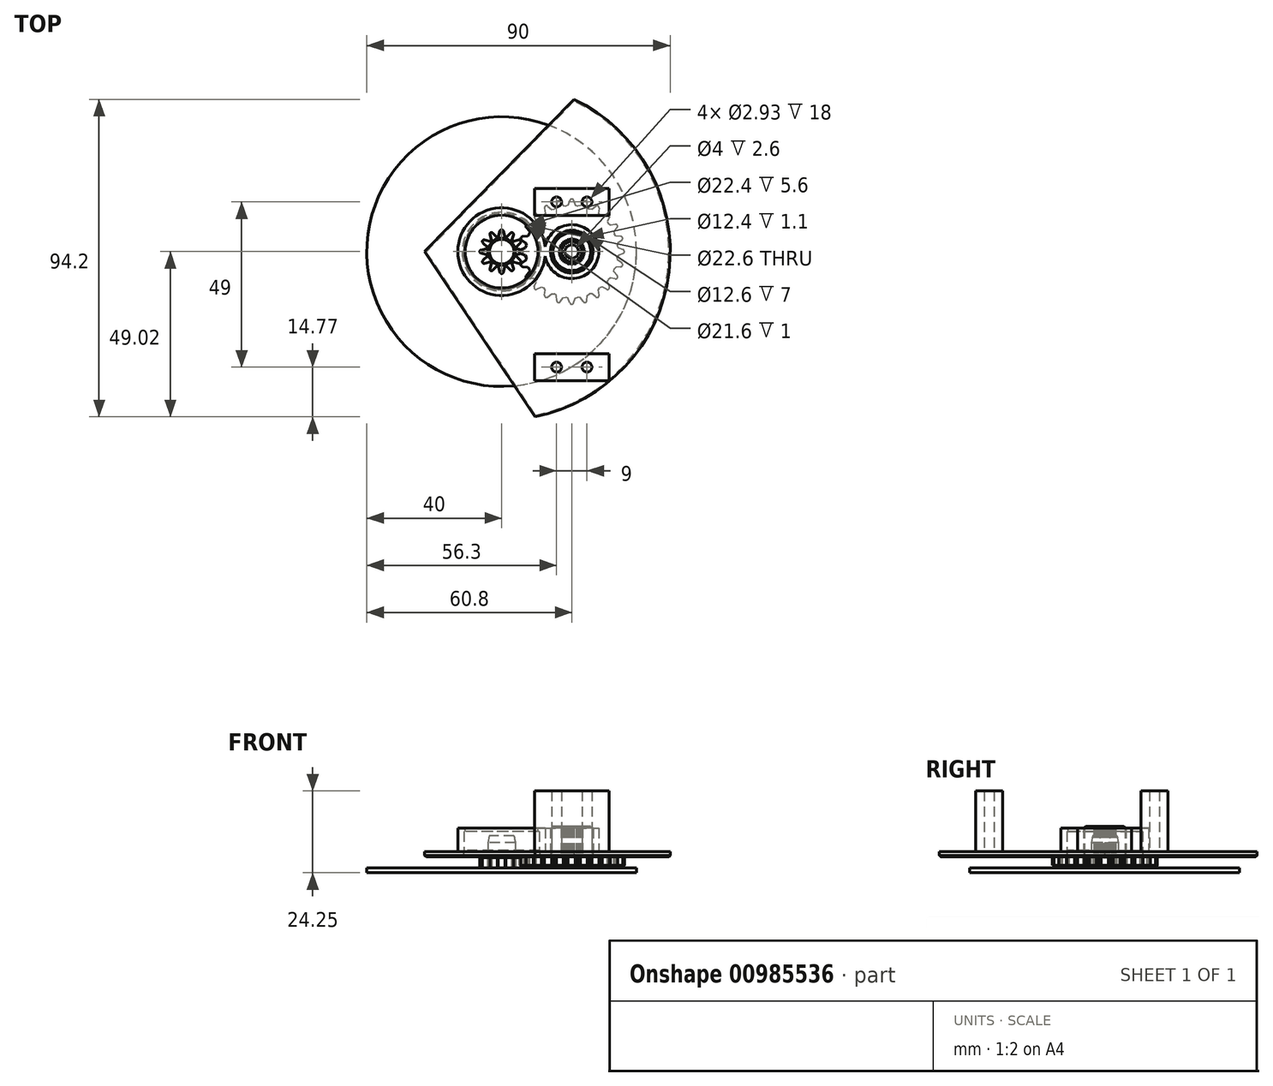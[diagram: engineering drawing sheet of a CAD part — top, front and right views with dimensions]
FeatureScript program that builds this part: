
annotation { "Feature Type Name" : "Feature", "Feature Type Description" : "" }
export const myFeature = defineFeature(function(context is Context, id is Id, definition is map)
    precondition{}
    {
        {
            var Q0;
            Q0=qCreatedBy(makeId("Top.planeOp"),FACE);
            var sketch = newSketch(context, id + "F0", { "sketchPlane" : qUnion([Q0])});
            skCircle(sketch, "E0", {"center": v(0, 0) * mm, "radius": 40 * mm});
            skSolve(sketch);
        }
        {
            var Q0;
            Q0=qSketchRegion(id+"F0",true);
            extrude(context, id + "F1", {"entities" : qUnion([Q0]), "depth" : 1.5 * mm, "offsetDistance" : 25 * mm});
        }
        {
            var Q0;
            Q0=makeQuery(id+"F1.opExtrude","CAP_FACE",FACE,{"disambiguationData":[OSD([sQuery(id+"F0.wireOp",EDGE,"E0")])],"isStart":false});
            var sketch = newSketch(context, id + "F2", { "sketchPlane" : qUnion([Q0])});
            skCircle(sketch, "E1", {"center": v(6, 0) * mm, "radius": 0.5 * mm});
            skLineSegment(sketch, "E2", {"start": v(6.13, 0.48) * mm, "end": v(4.2, 1) * mm});
            skLineSegment(sketch, "E3", {"start": v(4.2, 1) * mm, "end": v(3.85, 2.04) * mm});
            skLineSegment(sketch, "E4.MirrorCS", {"start": v(6.13, -0.48) * mm, "end": v(4.2, -1) * mm});
            skLineSegment(sketch, "E5.MirrorCS", {"start": v(4.2, -1) * mm, "end": v(3.85, -2.04) * mm});
            skCircle(sketch, "E6.1.0", {"center": v(5.2, 3) * mm, "radius": 0.5 * mm});
            skLineSegment(sketch, "E6.1.1", {"start": v(3.13, 2.97) * mm, "end": v(2.31, 3.69) * mm});
            skLineSegment(sketch, "E6.1.2", {"start": v(5.55, 2.65) * mm, "end": v(4.14, 1.23) * mm});
            skLineSegment(sketch, "E6.1.3", {"start": v(4.14, 1.23) * mm, "end": v(4.35, 0.16) * mm});
            skLineSegment(sketch, "E6.1.4", {"start": v(5.07, 3.48) * mm, "end": v(3.13, 2.97) * mm});
            skCircle(sketch, "E6.2.0", {"center": v(3, 5.2) * mm, "radius": 0.5 * mm});
            skLineSegment(sketch, "E6.2.1", {"start": v(1.23, 4.14) * mm, "end": v(0.16, 4.35) * mm});
            skLineSegment(sketch, "E6.2.2", {"start": v(3.48, 5.07) * mm, "end": v(2.97, 3.13) * mm});
            skLineSegment(sketch, "E6.2.3", {"start": v(2.97, 3.13) * mm, "end": v(3.69, 2.31) * mm});
            skLineSegment(sketch, "E6.2.4", {"start": v(2.65, 5.55) * mm, "end": v(1.23, 4.14) * mm});
            skCircle(sketch, "E6.3.0", {"center": v(0, 6) * mm, "radius": 0.5 * mm});
            skLineSegment(sketch, "E6.3.1", {"start": v(-1, 4.2) * mm, "end": v(-2.04, 3.85) * mm});
            skLineSegment(sketch, "E6.3.2", {"start": v(0.48, 6.13) * mm, "end": v(1, 4.2) * mm});
            skLineSegment(sketch, "E6.3.3", {"start": v(1, 4.2) * mm, "end": v(2.04, 3.85) * mm});
            skLineSegment(sketch, "E6.3.4", {"start": v(-0.48, 6.13) * mm, "end": v(-1, 4.2) * mm});
            skCircle(sketch, "E6.4.0", {"center": v(-3, 5.2) * mm, "radius": 0.5 * mm});
            skLineSegment(sketch, "E6.4.1", {"start": v(-2.97, 3.13) * mm, "end": v(-3.69, 2.31) * mm});
            skLineSegment(sketch, "E6.4.2", {"start": v(-2.65, 5.55) * mm, "end": v(-1.23, 4.14) * mm});
            skLineSegment(sketch, "E6.4.3", {"start": v(-1.23, 4.14) * mm, "end": v(-0.16, 4.35) * mm});
            skLineSegment(sketch, "E6.4.4", {"start": v(-3.48, 5.07) * mm, "end": v(-2.97, 3.13) * mm});
            skCircle(sketch, "E6.5.0", {"center": v(-5.2, 3) * mm, "radius": 0.5 * mm});
            skLineSegment(sketch, "E6.5.1", {"start": v(-4.14, 1.23) * mm, "end": v(-4.35, 0.16) * mm});
            skLineSegment(sketch, "E6.5.2", {"start": v(-5.07, 3.48) * mm, "end": v(-3.13, 2.97) * mm});
            skLineSegment(sketch, "E6.5.3", {"start": v(-3.13, 2.97) * mm, "end": v(-2.31, 3.69) * mm});
            skLineSegment(sketch, "E6.5.4", {"start": v(-5.55, 2.65) * mm, "end": v(-4.14, 1.23) * mm});
            skCircle(sketch, "E6.6.0", {"center": v(-6, 0) * mm, "radius": 0.5 * mm});
            skLineSegment(sketch, "E6.6.1", {"start": v(-4.2, -1) * mm, "end": v(-3.85, -2.04) * mm});
            skLineSegment(sketch, "E6.6.2", {"start": v(-6.13, 0.48) * mm, "end": v(-4.2, 1) * mm});
            skLineSegment(sketch, "E6.6.3", {"start": v(-4.2, 1) * mm, "end": v(-3.85, 2.04) * mm});
            skLineSegment(sketch, "E6.6.4", {"start": v(-6.13, -0.48) * mm, "end": v(-4.2, -1) * mm});
            skCircle(sketch, "E6.7.0", {"center": v(-5.2, -3) * mm, "radius": 0.5 * mm});
            skLineSegment(sketch, "E6.7.1", {"start": v(-3.13, -2.97) * mm, "end": v(-2.31, -3.69) * mm});
            skLineSegment(sketch, "E6.7.2", {"start": v(-5.55, -2.65) * mm, "end": v(-4.14, -1.23) * mm});
            skLineSegment(sketch, "E6.7.3", {"start": v(-4.14, -1.23) * mm, "end": v(-4.35, -0.16) * mm});
            skLineSegment(sketch, "E6.7.4", {"start": v(-5.07, -3.48) * mm, "end": v(-3.13, -2.97) * mm});
            skCircle(sketch, "E6.8.0", {"center": v(-3, -5.2) * mm, "radius": 0.5 * mm});
            skLineSegment(sketch, "E6.8.1", {"start": v(-1.23, -4.14) * mm, "end": v(-0.16, -4.35) * mm});
            skLineSegment(sketch, "E6.8.2", {"start": v(-3.48, -5.07) * mm, "end": v(-2.97, -3.13) * mm});
            skLineSegment(sketch, "E6.8.3", {"start": v(-2.97, -3.13) * mm, "end": v(-3.69, -2.31) * mm});
            skLineSegment(sketch, "E6.8.4", {"start": v(-2.65, -5.55) * mm, "end": v(-1.23, -4.14) * mm});
            skCircle(sketch, "E6.9.0", {"center": v(0, -6) * mm, "radius": 0.5 * mm});
            skLineSegment(sketch, "E6.9.1", {"start": v(1, -4.2) * mm, "end": v(2.04, -3.85) * mm});
            skLineSegment(sketch, "E6.9.2", {"start": v(-0.48, -6.13) * mm, "end": v(-1, -4.2) * mm});
            skLineSegment(sketch, "E6.9.3", {"start": v(-1, -4.2) * mm, "end": v(-2.04, -3.85) * mm});
            skLineSegment(sketch, "E6.9.4", {"start": v(0.48, -6.13) * mm, "end": v(1, -4.2) * mm});
            skPoint(sketch, "E6.center", {"position": v(0, 0) * mm});
            skLineSegment(sketch, "E7.2.10.0", {"start": v(2.97, -3.13) * mm, "end": v(3.69, -2.31) * mm});
            skLineSegment(sketch, "E7.5.10.0", {"start": v(2.65, -5.55) * mm, "end": v(1.23, -4.14) * mm});
            skLineSegment(sketch, "E7.8.10.0", {"start": v(1.23, -4.14) * mm, "end": v(0.16, -4.35) * mm});
            skCircle(sketch, "E7.10.10.0", {"center": v(3, -5.2) * mm, "radius": 0.5 * mm});
            skLineSegment(sketch, "E7.11.10.0", {"start": v(3.48, -5.07) * mm, "end": v(2.97, -3.13) * mm});
            skLineSegment(sketch, "E7.2.11.0", {"start": v(4.14, -1.23) * mm, "end": v(4.35, -0.16) * mm});
            skLineSegment(sketch, "E7.5.11.0", {"start": v(5.07, -3.48) * mm, "end": v(3.13, -2.97) * mm});
            skLineSegment(sketch, "E7.8.11.0", {"start": v(3.13, -2.97) * mm, "end": v(2.31, -3.69) * mm});
            skCircle(sketch, "E7.10.11.0", {"center": v(5.2, -3) * mm, "radius": 0.5 * mm});
            skLineSegment(sketch, "E7.11.11.0", {"start": v(5.55, -2.65) * mm, "end": v(4.14, -1.23) * mm});
            skSolve(sketch);
        }
        {
            var Q0;
            Q0=qSketchRegion(id+"F2",true);
            extrude(context, id + "F3", {"entities" : qUnion([Q0]), "operationType" : NewBodyOperationType.ADD, "depth" : 3 * mm, "offsetDistance" : 25 * mm});
        }
        {
            var Q0;
            Q0=makeQuery(id+"F3.opExtrude","CAP_FACE",FACE,{"disambiguationData":[OSD([sQuery(id+"F2.wireOp",EDGE,"E1"),sQuery(id+"F2.wireOp",EDGE,"E2"),sQuery(id+"F2.wireOp",EDGE,"E3"),sQuery(id+"F2.wireOp",EDGE,"E4.MirrorCS"),sQuery(id+"F2.wireOp",EDGE,"E5.MirrorCS"),sQuery(id+"F2.wireOp",EDGE,"E6.1.0"),sQuery(id+"F2.wireOp",EDGE,"E6.1.1"),sQuery(id+"F2.wireOp",EDGE,"E6.1.2"),sQuery(id+"F2.wireOp",EDGE,"E6.1.3"),sQuery(id+"F2.wireOp",EDGE,"E6.1.4"),sQuery(id+"F2.wireOp",EDGE,"E6.2.0"),sQuery(id+"F2.wireOp",EDGE,"E6.2.1"),sQuery(id+"F2.wireOp",EDGE,"E6.2.2"),sQuery(id+"F2.wireOp",EDGE,"E6.2.3"),sQuery(id+"F2.wireOp",EDGE,"E6.2.4"),sQuery(id+"F2.wireOp",EDGE,"E6.3.0"),sQuery(id+"F2.wireOp",EDGE,"E6.3.1"),sQuery(id+"F2.wireOp",EDGE,"E6.3.2"),sQuery(id+"F2.wireOp",EDGE,"E6.3.3"),sQuery(id+"F2.wireOp",EDGE,"E6.3.4"),sQuery(id+"F2.wireOp",EDGE,"E6.4.0"),sQuery(id+"F2.wireOp",EDGE,"E6.4.1"),sQuery(id+"F2.wireOp",EDGE,"E6.4.2"),sQuery(id+"F2.wireOp",EDGE,"E6.4.3"),sQuery(id+"F2.wireOp",EDGE,"E6.4.4"),sQuery(id+"F2.wireOp",EDGE,"E6.5.0"),sQuery(id+"F2.wireOp",EDGE,"E6.5.1"),sQuery(id+"F2.wireOp",EDGE,"E6.5.2"),sQuery(id+"F2.wireOp",EDGE,"E6.5.3"),sQuery(id+"F2.wireOp",EDGE,"E6.5.4"),sQuery(id+"F2.wireOp",EDGE,"E6.6.0"),sQuery(id+"F2.wireOp",EDGE,"E6.6.1"),sQuery(id+"F2.wireOp",EDGE,"E6.6.2"),sQuery(id+"F2.wireOp",EDGE,"E6.6.3"),sQuery(id+"F2.wireOp",EDGE,"E6.6.4"),sQuery(id+"F2.wireOp",EDGE,"E6.7.0"),sQuery(id+"F2.wireOp",EDGE,"E6.7.1"),sQuery(id+"F2.wireOp",EDGE,"E6.7.2"),sQuery(id+"F2.wireOp",EDGE,"E6.7.3"),sQuery(id+"F2.wireOp",EDGE,"E6.7.4"),sQuery(id+"F2.wireOp",EDGE,"E6.8.0"),sQuery(id+"F2.wireOp",EDGE,"E6.8.1"),sQuery(id+"F2.wireOp",EDGE,"E6.8.2"),sQuery(id+"F2.wireOp",EDGE,"E6.8.3"),sQuery(id+"F2.wireOp",EDGE,"E6.8.4"),sQuery(id+"F2.wireOp",EDGE,"E6.9.0"),sQuery(id+"F2.wireOp",EDGE,"E6.9.1"),sQuery(id+"F2.wireOp",EDGE,"E6.9.2"),sQuery(id+"F2.wireOp",EDGE,"E6.9.3"),sQuery(id+"F2.wireOp",EDGE,"E6.9.4"),sQuery(id+"F2.wireOp",EDGE,"E7.2.10.0"),sQuery(id+"F2.wireOp",EDGE,"E7.5.10.0"),sQuery(id+"F2.wireOp",EDGE,"E7.8.10.0"),sQuery(id+"F2.wireOp",EDGE,"E7.10.10.0"),sQuery(id+"F2.wireOp",EDGE,"E7.11.10.0"),sQuery(id+"F2.wireOp",EDGE,"E7.2.11.0"),sQuery(id+"F2.wireOp",EDGE,"E7.5.11.0"),sQuery(id+"F2.wireOp",EDGE,"E7.8.11.0"),sQuery(id+"F2.wireOp",EDGE,"E7.10.11.0"),sQuery(id+"F2.wireOp",EDGE,"E7.11.11.0")])],"isStart":false});
            var sketch = newSketch(context, id + "F4", { "sketchPlane" : qUnion([Q0])});
            skCircle(sketch, "E8", {"center": v(0, 0) * mm, "radius": 4.05 * mm});
            skSolve(sketch);
        }
        {
            var Q0;
            Q0=qSketchRegion(id+"F4",true);
            extrude(context, id + "F5", {"entities" : qUnion([Q0]), "operationType" : NewBodyOperationType.ADD, "depth" : 6.5 * mm, "offsetDistance" : 25 * mm});
        }
        {
            var Q0;
            Q0=makeQuery(id+"F5.opExtrude","CAP_EDGE",EDGE,{"disambiguationData":[OSD([sQuery(id+"F4.wireOp",EDGE,"E8")])],"isStart":false});
            chamfer(context, id + "F6", {"entities" : qUnion([Q0]), "chamferType" : ChamferType.TWO_OFFSETS, "width1" : .4 * mm, "oppositeDirection" : false, "width2" : 2 * mm, "tangentPropagation" : true});
        }
        {
            var Q0;
            Q0=makeQuery(id+"F5.opExtrude","CAP_FACE",FACE,{"disambiguationData":[OSD([sQuery(id+"F4.wireOp",EDGE,"E8")])],"isStart":false});
            cPlane(context, id + "F7", {"entities" : qUnion([Q0]), "cplaneType" : CPlaneType.OFFSET, "offset" : 6.25 * mm, "oppositeDirection" : true, "width" : 150 * mm, "height" : 150 * mm});
        }
        {
            var Q0;
            Q0=qCreatedBy(id+"F7.planeOp",FACE);
            var sketch = newSketch(context, id + "F8", { "sketchPlane" : qUnion([Q0])});
            skCircle(sketch, "E9", {"center": v(20.8, 0) * mm, "radius": 2 * mm});
            skCircle(sketch, "E10", {"center": v(35.8, 0) * mm, "radius": 0.6 * mm});
            skLineSegment(sketch, "E11", {"start": v(36, 0.56) * mm, "end": v(34.6, 1.08) * mm});
            skLineSegment(sketch, "E12", {"start": v(35.8, 0) * mm, "end": v(35.3, 0) * mm});
            skLineSegment(sketch, "E13", {"start": v(34.6, 1.08) * mm, "end": v(34.2, 2) * mm});
            skLineSegment(sketch, "E14.MirrorCS", {"start": v(36, -0.56) * mm, "end": v(34.6, -1.08) * mm});
            skLineSegment(sketch, "E15.MirrorCS", {"start": v(34.6, -1.08) * mm, "end": v(34.2, -2) * mm});
            skLineSegment(sketch, "E16.1.0", {"start": v(35.63, 3.4) * mm, "end": v(34.4, 2.53) * mm});
            skCircle(sketch, "E16.1.1", {"center": v(35.29, 3.88) * mm, "radius": 0.6 * mm});
            skLineSegment(sketch, "E16.1.2", {"start": v(35.34, 4.48) * mm, "end": v(33.85, 4.61) * mm});
            skLineSegment(sketch, "E16.1.3", {"start": v(34.4, 2.53) * mm, "end": v(34.25, 1.54) * mm});
            skLineSegment(sketch, "E16.1.4", {"start": v(33.85, 4.61) * mm, "end": v(33.22, 5.4) * mm});
            skLineSegment(sketch, "E16.1.5", {"start": v(35.29, 3.88) * mm, "end": v(34.8, 3.75) * mm});
            skLineSegment(sketch, "E16.2.0", {"start": v(34.25, 7.11) * mm, "end": v(33.29, 5.97) * mm});
            skCircle(sketch, "E16.2.1", {"center": v(33.8, 7.5) * mm, "radius": 0.6 * mm});
            skLineSegment(sketch, "E16.2.2", {"start": v(33.69, 8.1) * mm, "end": v(32.2, 7.83) * mm});
            skLineSegment(sketch, "E16.2.3", {"start": v(33.29, 5.97) * mm, "end": v(33.4, 4.97) * mm});
            skLineSegment(sketch, "E16.2.4", {"start": v(32.2, 7.83) * mm, "end": v(31.4, 8.42) * mm});
            skLineSegment(sketch, "E16.2.5", {"start": v(33.8, 7.5) * mm, "end": v(33.36, 7.25) * mm});
            skLineSegment(sketch, "E16.3.0", {"start": v(31.95, 10.35) * mm, "end": v(31.32, 9) * mm});
            skCircle(sketch, "E16.3.1", {"center": v(31.4, 10.6) * mm, "radius": 0.6 * mm});
            skLineSegment(sketch, "E16.3.2", {"start": v(31.15, 11.15) * mm, "end": v(29.8, 10.52) * mm});
            skLineSegment(sketch, "E16.3.3", {"start": v(31.32, 9) * mm, "end": v(31.68, 8.06) * mm});
            skLineSegment(sketch, "E16.3.4", {"start": v(29.8, 10.52) * mm, "end": v(28.86, 10.88) * mm});
            skLineSegment(sketch, "E16.3.5", {"start": v(31.4, 10.6) * mm, "end": v(31.05, 10.25) * mm});
            skLineSegment(sketch, "E16.4.0", {"start": v(28.9, 12.89) * mm, "end": v(28.63, 11.4) * mm});
            skCircle(sketch, "E16.4.1", {"center": v(28.3, 13) * mm, "radius": 0.6 * mm});
            skLineSegment(sketch, "E16.4.2", {"start": v(27.91, 13.45) * mm, "end": v(26.77, 12.49) * mm});
            skLineSegment(sketch, "E16.4.3", {"start": v(28.63, 11.4) * mm, "end": v(29.22, 10.6) * mm});
            skLineSegment(sketch, "E16.4.4", {"start": v(26.77, 12.49) * mm, "end": v(25.77, 12.6) * mm});
            skLineSegment(sketch, "E16.4.5", {"start": v(28.3, 13) * mm, "end": v(28.05, 12.56) * mm});
            skLineSegment(sketch, "E16.5.0", {"start": v(25.28, 14.54) * mm, "end": v(25.41, 13.05) * mm});
            skCircle(sketch, "E16.5.1", {"center": v(24.68, 14.49) * mm, "radius": 0.6 * mm});
            skLineSegment(sketch, "E16.5.2", {"start": v(24.2, 14.83) * mm, "end": v(23.33, 13.6) * mm});
            skLineSegment(sketch, "E16.5.3", {"start": v(25.41, 13.05) * mm, "end": v(26.2, 12.42) * mm});
            skLineSegment(sketch, "E16.5.4", {"start": v(23.33, 13.6) * mm, "end": v(22.34, 13.45) * mm});
            skLineSegment(sketch, "E16.5.5", {"start": v(24.68, 14.49) * mm, "end": v(24.55, 14) * mm});
            skLineSegment(sketch, "E16.6.0", {"start": v(21.36, 15.2) * mm, "end": v(21.88, 13.8) * mm});
            skCircle(sketch, "E16.6.1", {"center": v(20.8, 15) * mm, "radius": 0.6 * mm});
            skLineSegment(sketch, "E16.6.2", {"start": v(20.24, 15.2) * mm, "end": v(19.72, 13.8) * mm});
            skLineSegment(sketch, "E16.6.3", {"start": v(21.88, 13.8) * mm, "end": v(22.8, 13.4) * mm});
            skLineSegment(sketch, "E16.6.4", {"start": v(19.72, 13.8) * mm, "end": v(18.8, 13.4) * mm});
            skLineSegment(sketch, "E16.6.5", {"start": v(20.8, 15) * mm, "end": v(20.8, 14.5) * mm});
            skLineSegment(sketch, "E16.7.0", {"start": v(17.4, 14.83) * mm, "end": v(18.27, 13.6) * mm});
            skCircle(sketch, "E16.7.1", {"center": v(16.92, 14.49) * mm, "radius": 0.6 * mm});
            skLineSegment(sketch, "E16.7.2", {"start": v(16.32, 14.54) * mm, "end": v(16.19, 13.05) * mm});
            skLineSegment(sketch, "E16.7.3", {"start": v(18.27, 13.6) * mm, "end": v(19.26, 13.45) * mm});
            skLineSegment(sketch, "E16.7.4", {"start": v(16.19, 13.05) * mm, "end": v(15.4, 12.42) * mm});
            skLineSegment(sketch, "E16.7.5", {"start": v(16.92, 14.49) * mm, "end": v(17.05, 14) * mm});
            skLineSegment(sketch, "E16.8.0", {"start": v(13.69, 13.45) * mm, "end": v(14.83, 12.49) * mm});
            skCircle(sketch, "E16.8.1", {"center": v(13.3, 13) * mm, "radius": 0.6 * mm});
            skLineSegment(sketch, "E16.8.2", {"start": v(12.7, 12.89) * mm, "end": v(12.97, 11.4) * mm});
            skLineSegment(sketch, "E16.8.3", {"start": v(14.83, 12.49) * mm, "end": v(15.83, 12.6) * mm});
            skLineSegment(sketch, "E16.8.4", {"start": v(12.97, 11.4) * mm, "end": v(12.38, 10.6) * mm});
            skLineSegment(sketch, "E16.8.5", {"start": v(13.3, 13) * mm, "end": v(13.55, 12.56) * mm});
            skLineSegment(sketch, "E16.9.0", {"start": v(10.45, 11.15) * mm, "end": v(11.8, 10.52) * mm});
            skCircle(sketch, "E16.9.1", {"center": v(10.2, 10.6) * mm, "radius": 0.6 * mm});
            skLineSegment(sketch, "E16.9.2", {"start": v(9.65, 10.35) * mm, "end": v(10.28, 9) * mm});
            skLineSegment(sketch, "E16.9.3", {"start": v(11.8, 10.52) * mm, "end": v(12.74, 10.88) * mm});
            skLineSegment(sketch, "E16.9.4", {"start": v(10.28, 9) * mm, "end": v(9.92, 8.06) * mm});
            skLineSegment(sketch, "E16.9.5", {"start": v(10.2, 10.6) * mm, "end": v(10.55, 10.25) * mm});
            skLineSegment(sketch, "E16.10.0", {"start": v(7.91, 8.1) * mm, "end": v(9.4, 7.83) * mm});
            skCircle(sketch, "E16.10.1", {"center": v(7.8, 7.5) * mm, "radius": 0.6 * mm});
            skLineSegment(sketch, "E16.10.2", {"start": v(7.35, 7.11) * mm, "end": v(8.31, 5.97) * mm});
            skLineSegment(sketch, "E16.10.3", {"start": v(9.4, 7.83) * mm, "end": v(10.2, 8.42) * mm});
            skLineSegment(sketch, "E16.10.4", {"start": v(8.31, 5.97) * mm, "end": v(8.2, 4.97) * mm});
            skLineSegment(sketch, "E16.10.5", {"start": v(7.8, 7.5) * mm, "end": v(8.24, 7.25) * mm});
            skLineSegment(sketch, "E16.11.0", {"start": v(6.26, 4.48) * mm, "end": v(7.75, 4.61) * mm});
            skCircle(sketch, "E16.11.1", {"center": v(6.31, 3.88) * mm, "radius": 0.6 * mm});
            skLineSegment(sketch, "E16.11.2", {"start": v(5.97, 3.4) * mm, "end": v(7.2, 2.53) * mm});
            skLineSegment(sketch, "E16.11.3", {"start": v(7.75, 4.61) * mm, "end": v(8.38, 5.4) * mm});
            skLineSegment(sketch, "E16.11.4", {"start": v(7.2, 2.53) * mm, "end": v(7.35, 1.54) * mm});
            skLineSegment(sketch, "E16.11.5", {"start": v(6.31, 3.88) * mm, "end": v(6.8, 3.75) * mm});
            skLineSegment(sketch, "E16.12.0", {"start": v(5.6, 0.56) * mm, "end": v(7, 1.08) * mm});
            skCircle(sketch, "E16.12.1", {"center": v(5.8, 0) * mm, "radius": 0.6 * mm});
            skLineSegment(sketch, "E16.12.2", {"start": v(5.6, -0.56) * mm, "end": v(7, -1.08) * mm});
            skLineSegment(sketch, "E16.12.3", {"start": v(7, 1.08) * mm, "end": v(7.4, 2) * mm});
            skLineSegment(sketch, "E16.12.4", {"start": v(7, -1.08) * mm, "end": v(7.4, -2) * mm});
            skLineSegment(sketch, "E16.12.5", {"start": v(5.8, 0) * mm, "end": v(6.3, 0) * mm});
            skLineSegment(sketch, "E16.13.0", {"start": v(5.97, -3.4) * mm, "end": v(7.2, -2.53) * mm});
            skCircle(sketch, "E16.13.1", {"center": v(6.31, -3.88) * mm, "radius": 0.6 * mm});
            skLineSegment(sketch, "E16.13.2", {"start": v(6.26, -4.48) * mm, "end": v(7.75, -4.61) * mm});
            skLineSegment(sketch, "E16.13.3", {"start": v(7.2, -2.53) * mm, "end": v(7.35, -1.54) * mm});
            skLineSegment(sketch, "E16.13.4", {"start": v(7.75, -4.61) * mm, "end": v(8.38, -5.4) * mm});
            skLineSegment(sketch, "E16.13.5", {"start": v(6.31, -3.88) * mm, "end": v(6.8, -3.75) * mm});
            skLineSegment(sketch, "E16.14.0", {"start": v(7.35, -7.11) * mm, "end": v(8.31, -5.97) * mm});
            skCircle(sketch, "E16.14.1", {"center": v(7.8, -7.5) * mm, "radius": 0.6 * mm});
            skLineSegment(sketch, "E16.14.2", {"start": v(7.91, -8.1) * mm, "end": v(9.4, -7.83) * mm});
            skLineSegment(sketch, "E16.14.3", {"start": v(8.31, -5.97) * mm, "end": v(8.2, -4.97) * mm});
            skLineSegment(sketch, "E16.14.4", {"start": v(9.4, -7.83) * mm, "end": v(10.2, -8.42) * mm});
            skLineSegment(sketch, "E16.14.5", {"start": v(7.8, -7.5) * mm, "end": v(8.24, -7.25) * mm});
            skLineSegment(sketch, "E16.15.0", {"start": v(9.65, -10.35) * mm, "end": v(10.28, -9) * mm});
            skCircle(sketch, "E16.15.1", {"center": v(10.2, -10.6) * mm, "radius": 0.6 * mm});
            skLineSegment(sketch, "E16.15.2", {"start": v(10.45, -11.15) * mm, "end": v(11.8, -10.52) * mm});
            skLineSegment(sketch, "E16.15.3", {"start": v(10.28, -9) * mm, "end": v(9.92, -8.06) * mm});
            skLineSegment(sketch, "E16.15.4", {"start": v(11.8, -10.52) * mm, "end": v(12.74, -10.88) * mm});
            skLineSegment(sketch, "E16.15.5", {"start": v(10.2, -10.6) * mm, "end": v(10.55, -10.25) * mm});
            skLineSegment(sketch, "E16.16.0", {"start": v(12.7, -12.89) * mm, "end": v(12.97, -11.4) * mm});
            skCircle(sketch, "E16.16.1", {"center": v(13.3, -13) * mm, "radius": 0.6 * mm});
            skLineSegment(sketch, "E16.16.2", {"start": v(13.69, -13.45) * mm, "end": v(14.83, -12.49) * mm});
            skLineSegment(sketch, "E16.16.3", {"start": v(12.97, -11.4) * mm, "end": v(12.38, -10.6) * mm});
            skLineSegment(sketch, "E16.16.4", {"start": v(14.83, -12.49) * mm, "end": v(15.83, -12.6) * mm});
            skLineSegment(sketch, "E16.16.5", {"start": v(13.3, -13) * mm, "end": v(13.55, -12.56) * mm});
            skLineSegment(sketch, "E16.17.0", {"start": v(16.32, -14.54) * mm, "end": v(16.19, -13.05) * mm});
            skCircle(sketch, "E16.17.1", {"center": v(16.92, -14.49) * mm, "radius": 0.6 * mm});
            skLineSegment(sketch, "E16.17.2", {"start": v(17.4, -14.83) * mm, "end": v(18.27, -13.6) * mm});
            skLineSegment(sketch, "E16.17.3", {"start": v(16.19, -13.05) * mm, "end": v(15.4, -12.42) * mm});
            skLineSegment(sketch, "E16.17.4", {"start": v(18.27, -13.6) * mm, "end": v(19.26, -13.45) * mm});
            skLineSegment(sketch, "E16.17.5", {"start": v(16.92, -14.49) * mm, "end": v(17.05, -14) * mm});
            skLineSegment(sketch, "E16.18.0", {"start": v(20.24, -15.2) * mm, "end": v(19.72, -13.8) * mm});
            skCircle(sketch, "E16.18.1", {"center": v(20.8, -15) * mm, "radius": 0.6 * mm});
            skLineSegment(sketch, "E16.18.2", {"start": v(21.36, -15.2) * mm, "end": v(21.88, -13.8) * mm});
            skLineSegment(sketch, "E16.18.3", {"start": v(19.72, -13.8) * mm, "end": v(18.8, -13.4) * mm});
            skLineSegment(sketch, "E16.18.4", {"start": v(21.88, -13.8) * mm, "end": v(22.8, -13.4) * mm});
            skLineSegment(sketch, "E16.18.5", {"start": v(20.8, -15) * mm, "end": v(20.8, -14.5) * mm});
            skLineSegment(sketch, "E16.19.0", {"start": v(24.2, -14.83) * mm, "end": v(23.33, -13.6) * mm});
            skCircle(sketch, "E16.19.1", {"center": v(24.68, -14.49) * mm, "radius": 0.6 * mm});
            skLineSegment(sketch, "E16.19.2", {"start": v(25.28, -14.54) * mm, "end": v(25.41, -13.05) * mm});
            skLineSegment(sketch, "E16.19.3", {"start": v(23.33, -13.6) * mm, "end": v(22.34, -13.45) * mm});
            skLineSegment(sketch, "E16.19.4", {"start": v(25.41, -13.05) * mm, "end": v(26.2, -12.42) * mm});
            skLineSegment(sketch, "E16.19.5", {"start": v(24.68, -14.49) * mm, "end": v(24.55, -14) * mm});
            skLineSegment(sketch, "E16.20.0", {"start": v(27.91, -13.45) * mm, "end": v(26.77, -12.49) * mm});
            skCircle(sketch, "E16.20.1", {"center": v(28.3, -13) * mm, "radius": 0.6 * mm});
            skLineSegment(sketch, "E16.20.2", {"start": v(28.9, -12.89) * mm, "end": v(28.63, -11.4) * mm});
            skLineSegment(sketch, "E16.20.3", {"start": v(26.77, -12.49) * mm, "end": v(25.77, -12.6) * mm});
            skLineSegment(sketch, "E16.20.4", {"start": v(28.63, -11.4) * mm, "end": v(29.22, -10.6) * mm});
            skLineSegment(sketch, "E16.20.5", {"start": v(28.3, -13) * mm, "end": v(28.05, -12.56) * mm});
            skLineSegment(sketch, "E16.21.0", {"start": v(31.15, -11.15) * mm, "end": v(29.8, -10.52) * mm});
            skCircle(sketch, "E16.21.1", {"center": v(31.4, -10.6) * mm, "radius": 0.6 * mm});
            skLineSegment(sketch, "E16.21.2", {"start": v(31.95, -10.35) * mm, "end": v(31.32, -9) * mm});
            skLineSegment(sketch, "E16.21.3", {"start": v(29.8, -10.52) * mm, "end": v(28.86, -10.88) * mm});
            skLineSegment(sketch, "E16.21.4", {"start": v(31.32, -9) * mm, "end": v(31.68, -8.06) * mm});
            skLineSegment(sketch, "E16.21.5", {"start": v(31.4, -10.6) * mm, "end": v(31.05, -10.25) * mm});
            skLineSegment(sketch, "E16.22.0", {"start": v(33.69, -8.1) * mm, "end": v(32.2, -7.83) * mm});
            skCircle(sketch, "E16.22.1", {"center": v(33.8, -7.5) * mm, "radius": 0.6 * mm});
            skLineSegment(sketch, "E16.22.2", {"start": v(34.25, -7.11) * mm, "end": v(33.29, -5.97) * mm});
            skLineSegment(sketch, "E16.22.3", {"start": v(32.2, -7.83) * mm, "end": v(31.4, -8.42) * mm});
            skLineSegment(sketch, "E16.22.4", {"start": v(33.29, -5.97) * mm, "end": v(33.4, -4.97) * mm});
            skLineSegment(sketch, "E16.22.5", {"start": v(33.8, -7.5) * mm, "end": v(33.36, -7.25) * mm});
            skLineSegment(sketch, "E16.23.0", {"start": v(35.34, -4.48) * mm, "end": v(33.85, -4.61) * mm});
            skCircle(sketch, "E16.23.1", {"center": v(35.29, -3.88) * mm, "radius": 0.6 * mm});
            skLineSegment(sketch, "E16.23.2", {"start": v(35.63, -3.4) * mm, "end": v(34.4, -2.53) * mm});
            skLineSegment(sketch, "E16.23.3", {"start": v(33.85, -4.61) * mm, "end": v(33.22, -5.4) * mm});
            skLineSegment(sketch, "E16.23.4", {"start": v(34.4, -2.53) * mm, "end": v(34.25, -1.54) * mm});
            skLineSegment(sketch, "E16.23.5", {"start": v(35.29, -3.88) * mm, "end": v(34.8, -3.75) * mm});
            skSolve(sketch);
        }
        {
            var Q0;
            Q0=qSketchRegion(id+"F8",true);
            extrude(context, id + "F9", {"entities" : qUnion([Q0]), "oppositeDirection" : true, "depth" : 2.6 * mm, "offsetDistance" : 25 * mm});
        }
        {
            var Q0;
            Q0=makeQuery(id+"F9.opExtrude","CAP_FACE",FACE,{"disambiguationData":[OSD([sQuery(id+"F8.wireOp",EDGE,"E9"),sQuery(id+"F8.wireOp",EDGE,"E10"),sQuery(id+"F8.wireOp",EDGE,"E11"),sQuery(id+"F8.wireOp",EDGE,"E13"),sQuery(id+"F8.wireOp",EDGE,"E14.MirrorCS"),sQuery(id+"F8.wireOp",EDGE,"E15.MirrorCS"),sQuery(id+"F8.wireOp",EDGE,"E16.1.0"),sQuery(id+"F8.wireOp",EDGE,"E16.1.1"),sQuery(id+"F8.wireOp",EDGE,"E16.1.2"),sQuery(id+"F8.wireOp",EDGE,"E16.1.3"),sQuery(id+"F8.wireOp",EDGE,"E16.1.4"),sQuery(id+"F8.wireOp",EDGE,"E16.2.0"),sQuery(id+"F8.wireOp",EDGE,"E16.2.1"),sQuery(id+"F8.wireOp",EDGE,"E16.2.2"),sQuery(id+"F8.wireOp",EDGE,"E16.2.3"),sQuery(id+"F8.wireOp",EDGE,"E16.2.4"),sQuery(id+"F8.wireOp",EDGE,"E16.3.0"),sQuery(id+"F8.wireOp",EDGE,"E16.3.1"),sQuery(id+"F8.wireOp",EDGE,"E16.3.2"),sQuery(id+"F8.wireOp",EDGE,"E16.3.3"),sQuery(id+"F8.wireOp",EDGE,"E16.3.4"),sQuery(id+"F8.wireOp",EDGE,"E16.4.0"),sQuery(id+"F8.wireOp",EDGE,"E16.4.1"),sQuery(id+"F8.wireOp",EDGE,"E16.4.2"),sQuery(id+"F8.wireOp",EDGE,"E16.4.3"),sQuery(id+"F8.wireOp",EDGE,"E16.4.4"),sQuery(id+"F8.wireOp",EDGE,"E16.5.0"),sQuery(id+"F8.wireOp",EDGE,"E16.5.1"),sQuery(id+"F8.wireOp",EDGE,"E16.5.2"),sQuery(id+"F8.wireOp",EDGE,"E16.5.3"),sQuery(id+"F8.wireOp",EDGE,"E16.5.4"),sQuery(id+"F8.wireOp",EDGE,"E16.6.0"),sQuery(id+"F8.wireOp",EDGE,"E16.6.1"),sQuery(id+"F8.wireOp",EDGE,"E16.6.2"),sQuery(id+"F8.wireOp",EDGE,"E16.6.3"),sQuery(id+"F8.wireOp",EDGE,"E16.6.4"),sQuery(id+"F8.wireOp",EDGE,"E16.7.0"),sQuery(id+"F8.wireOp",EDGE,"E16.7.1"),sQuery(id+"F8.wireOp",EDGE,"E16.7.2"),sQuery(id+"F8.wireOp",EDGE,"E16.7.3"),sQuery(id+"F8.wireOp",EDGE,"E16.7.4"),sQuery(id+"F8.wireOp",EDGE,"E16.8.0"),sQuery(id+"F8.wireOp",EDGE,"E16.8.1"),sQuery(id+"F8.wireOp",EDGE,"E16.8.2"),sQuery(id+"F8.wireOp",EDGE,"E16.8.3"),sQuery(id+"F8.wireOp",EDGE,"E16.8.4"),sQuery(id+"F8.wireOp",EDGE,"E16.9.0"),sQuery(id+"F8.wireOp",EDGE,"E16.9.1"),sQuery(id+"F8.wireOp",EDGE,"E16.9.2"),sQuery(id+"F8.wireOp",EDGE,"E16.9.3"),sQuery(id+"F8.wireOp",EDGE,"E16.9.4"),sQuery(id+"F8.wireOp",EDGE,"E16.10.0"),sQuery(id+"F8.wireOp",EDGE,"E16.10.1"),sQuery(id+"F8.wireOp",EDGE,"E16.10.2"),sQuery(id+"F8.wireOp",EDGE,"E16.10.3"),sQuery(id+"F8.wireOp",EDGE,"E16.10.4"),sQuery(id+"F8.wireOp",EDGE,"E16.11.0"),sQuery(id+"F8.wireOp",EDGE,"E16.11.1"),sQuery(id+"F8.wireOp",EDGE,"E16.11.2"),sQuery(id+"F8.wireOp",EDGE,"E16.11.3"),sQuery(id+"F8.wireOp",EDGE,"E16.11.4"),sQuery(id+"F8.wireOp",EDGE,"E16.12.0"),sQuery(id+"F8.wireOp",EDGE,"E16.12.1"),sQuery(id+"F8.wireOp",EDGE,"E16.12.2"),sQuery(id+"F8.wireOp",EDGE,"E16.12.3"),sQuery(id+"F8.wireOp",EDGE,"E16.12.4"),sQuery(id+"F8.wireOp",EDGE,"E16.13.0"),sQuery(id+"F8.wireOp",EDGE,"E16.13.1"),sQuery(id+"F8.wireOp",EDGE,"E16.13.2"),sQuery(id+"F8.wireOp",EDGE,"E16.13.3"),sQuery(id+"F8.wireOp",EDGE,"E16.13.4"),sQuery(id+"F8.wireOp",EDGE,"E16.14.0"),sQuery(id+"F8.wireOp",EDGE,"E16.14.1"),sQuery(id+"F8.wireOp",EDGE,"E16.14.2"),sQuery(id+"F8.wireOp",EDGE,"E16.14.3"),sQuery(id+"F8.wireOp",EDGE,"E16.14.4"),sQuery(id+"F8.wireOp",EDGE,"E16.15.0"),sQuery(id+"F8.wireOp",EDGE,"E16.15.1"),sQuery(id+"F8.wireOp",EDGE,"E16.15.2"),sQuery(id+"F8.wireOp",EDGE,"E16.15.3"),sQuery(id+"F8.wireOp",EDGE,"E16.15.4"),sQuery(id+"F8.wireOp",EDGE,"E16.16.0"),sQuery(id+"F8.wireOp",EDGE,"E16.16.1"),sQuery(id+"F8.wireOp",EDGE,"E16.16.2"),sQuery(id+"F8.wireOp",EDGE,"E16.16.3"),sQuery(id+"F8.wireOp",EDGE,"E16.16.4"),sQuery(id+"F8.wireOp",EDGE,"E16.17.0"),sQuery(id+"F8.wireOp",EDGE,"E16.17.1"),sQuery(id+"F8.wireOp",EDGE,"E16.17.2"),sQuery(id+"F8.wireOp",EDGE,"E16.17.3"),sQuery(id+"F8.wireOp",EDGE,"E16.17.4"),sQuery(id+"F8.wireOp",EDGE,"E16.18.0"),sQuery(id+"F8.wireOp",EDGE,"E16.18.1"),sQuery(id+"F8.wireOp",EDGE,"E16.18.2"),sQuery(id+"F8.wireOp",EDGE,"E16.18.3"),sQuery(id+"F8.wireOp",EDGE,"E16.18.4"),sQuery(id+"F8.wireOp",EDGE,"E16.19.0"),sQuery(id+"F8.wireOp",EDGE,"E16.19.1"),sQuery(id+"F8.wireOp",EDGE,"E16.19.2"),sQuery(id+"F8.wireOp",EDGE,"E16.19.3"),sQuery(id+"F8.wireOp",EDGE,"E16.19.4"),sQuery(id+"F8.wireOp",EDGE,"E16.20.0"),sQuery(id+"F8.wireOp",EDGE,"E16.20.1"),sQuery(id+"F8.wireOp",EDGE,"E16.20.2"),sQuery(id+"F8.wireOp",EDGE,"E16.20.3"),sQuery(id+"F8.wireOp",EDGE,"E16.20.4"),sQuery(id+"F8.wireOp",EDGE,"E16.21.0"),sQuery(id+"F8.wireOp",EDGE,"E16.21.1"),sQuery(id+"F8.wireOp",EDGE,"E16.21.2"),sQuery(id+"F8.wireOp",EDGE,"E16.21.3"),sQuery(id+"F8.wireOp",EDGE,"E16.21.4"),sQuery(id+"F8.wireOp",EDGE,"E16.22.0"),sQuery(id+"F8.wireOp",EDGE,"E16.22.1"),sQuery(id+"F8.wireOp",EDGE,"E16.22.2"),sQuery(id+"F8.wireOp",EDGE,"E16.22.3"),sQuery(id+"F8.wireOp",EDGE,"E16.22.4"),sQuery(id+"F8.wireOp",EDGE,"E16.23.0"),sQuery(id+"F8.wireOp",EDGE,"E16.23.1"),sQuery(id+"F8.wireOp",EDGE,"E16.23.2"),sQuery(id+"F8.wireOp",EDGE,"E16.23.3"),sQuery(id+"F8.wireOp",EDGE,"E16.23.4")])],"isStart":true});
            var sketch = newSketch(context, id + "F10", { "sketchPlane" : qUnion([Q0])});
            skCircle(sketch, "E17", {"center": v(20.8, 0) * mm, "radius": 6 * mm});
            skLineSegment(sketch, "E18", {"start": v(23.5, 0) * mm, "end": v(24, 0.43) * mm});
            skLineSegment(sketch, "E19.MirrorCS", {"start": v(23.5, 0) * mm, "end": v(24, -0.4) * mm});
            skLineSegment(sketch, "E20.1.0", {"start": v(23.4, 0.7) * mm, "end": v(23.78, 1.25) * mm});
            skLineSegment(sketch, "E20.1.1", {"start": v(23.4, 0.7) * mm, "end": v(24, 0.43) * mm});
            skLineSegment(sketch, "E20.2.0", {"start": v(23.14, 1.35) * mm, "end": v(23.35, 1.98) * mm});
            skLineSegment(sketch, "E20.2.1", {"start": v(23.14, 1.35) * mm, "end": v(23.78, 1.25) * mm});
            skLineSegment(sketch, "E20.3.0", {"start": v(22.7, 1.9) * mm, "end": v(22.76, 2.57) * mm});
            skLineSegment(sketch, "E20.3.1", {"start": v(22.7, 1.9) * mm, "end": v(23.35, 1.98) * mm});
            skLineSegment(sketch, "E20.4.0", {"start": v(22.15, 2.34) * mm, "end": v(22.02, 2.99) * mm});
            skLineSegment(sketch, "E20.4.1", {"start": v(22.15, 2.34) * mm, "end": v(22.76, 2.57) * mm});
            skLineSegment(sketch, "E20.5.0", {"start": v(21.5, 2.6) * mm, "end": v(21.2, 3.2) * mm});
            skLineSegment(sketch, "E20.5.1", {"start": v(21.5, 2.6) * mm, "end": v(22.02, 2.99) * mm});
            skLineSegment(sketch, "E20.6.0", {"start": v(20.8, 2.7) * mm, "end": v(20.37, 3.2) * mm});
            skLineSegment(sketch, "E20.6.1", {"start": v(20.8, 2.7) * mm, "end": v(21.2, 3.2) * mm});
            skLineSegment(sketch, "E20.7.0", {"start": v(20.1, 2.6) * mm, "end": v(19.55, 2.98) * mm});
            skLineSegment(sketch, "E20.7.1", {"start": v(20.1, 2.6) * mm, "end": v(20.37, 3.2) * mm});
            skLineSegment(sketch, "E20.8.0", {"start": v(19.45, 2.34) * mm, "end": v(18.82, 2.55) * mm});
            skLineSegment(sketch, "E20.8.1", {"start": v(19.45, 2.34) * mm, "end": v(19.55, 2.98) * mm});
            skLineSegment(sketch, "E20.9.0", {"start": v(18.9, 1.9) * mm, "end": v(18.23, 1.96) * mm});
            skLineSegment(sketch, "E20.9.1", {"start": v(18.9, 1.9) * mm, "end": v(18.82, 2.55) * mm});
            skLineSegment(sketch, "E20.10.0", {"start": v(18.46, 1.35) * mm, "end": v(17.81, 1.22) * mm});
            skLineSegment(sketch, "E20.10.1", {"start": v(18.46, 1.35) * mm, "end": v(18.23, 1.96) * mm});
            skLineSegment(sketch, "E20.11.0", {"start": v(18.2, 0.7) * mm, "end": v(17.6, 0.4) * mm});
            skLineSegment(sketch, "E20.11.1", {"start": v(18.2, 0.7) * mm, "end": v(17.81, 1.22) * mm});
            skLineSegment(sketch, "E20.12.0", {"start": v(18.1, 0) * mm, "end": v(17.6, -0.43) * mm});
            skLineSegment(sketch, "E20.12.1", {"start": v(18.1, 0) * mm, "end": v(17.6, 0.4) * mm});
            skLineSegment(sketch, "E20.13.0", {"start": v(18.2, -0.7) * mm, "end": v(17.82, -1.25) * mm});
            skLineSegment(sketch, "E20.13.1", {"start": v(18.2, -0.7) * mm, "end": v(17.6, -0.43) * mm});
            skLineSegment(sketch, "E20.14.0", {"start": v(18.46, -1.35) * mm, "end": v(18.25, -1.98) * mm});
            skLineSegment(sketch, "E20.14.1", {"start": v(18.46, -1.35) * mm, "end": v(17.82, -1.25) * mm});
            skLineSegment(sketch, "E21.1.15.0", {"start": v(18.9, -1.9) * mm, "end": v(18.84, -2.57) * mm});
            skLineSegment(sketch, "E21.3.15.0", {"start": v(18.9, -1.9) * mm, "end": v(18.25, -1.98) * mm});
            skLineSegment(sketch, "E21.1.16.0", {"start": v(19.45, -2.34) * mm, "end": v(19.58, -2.99) * mm});
            skLineSegment(sketch, "E21.3.16.0", {"start": v(19.45, -2.34) * mm, "end": v(18.84, -2.57) * mm});
            skLineSegment(sketch, "E21.1.17.0", {"start": v(20.1, -2.6) * mm, "end": v(20.4, -3.2) * mm});
            skLineSegment(sketch, "E21.3.17.0", {"start": v(20.1, -2.6) * mm, "end": v(19.58, -2.99) * mm});
            skLineSegment(sketch, "E21.1.18.0", {"start": v(20.8, -2.7) * mm, "end": v(21.23, -3.2) * mm});
            skLineSegment(sketch, "E21.3.18.0", {"start": v(20.8, -2.7) * mm, "end": v(20.4, -3.2) * mm});
            skLineSegment(sketch, "E21.1.19.0", {"start": v(21.5, -2.6) * mm, "end": v(22.05, -2.98) * mm});
            skLineSegment(sketch, "E21.3.19.0", {"start": v(21.5, -2.6) * mm, "end": v(21.23, -3.2) * mm});
            skLineSegment(sketch, "E21.1.20.0", {"start": v(22.15, -2.34) * mm, "end": v(22.78, -2.55) * mm});
            skLineSegment(sketch, "E21.3.20.0", {"start": v(22.15, -2.34) * mm, "end": v(22.05, -2.98) * mm});
            skLineSegment(sketch, "E21.1.21.0", {"start": v(22.7, -1.9) * mm, "end": v(23.37, -1.96) * mm});
            skLineSegment(sketch, "E21.3.21.0", {"start": v(22.7, -1.9) * mm, "end": v(22.78, -2.55) * mm});
            skLineSegment(sketch, "E21.1.22.0", {"start": v(23.14, -1.35) * mm, "end": v(23.79, -1.22) * mm});
            skLineSegment(sketch, "E21.3.22.0", {"start": v(23.14, -1.35) * mm, "end": v(23.37, -1.96) * mm});
            skLineSegment(sketch, "E21.1.23.0", {"start": v(23.4, -0.7) * mm, "end": v(24, -0.4) * mm});
            skLineSegment(sketch, "E21.3.23.0", {"start": v(23.4, -0.7) * mm, "end": v(23.79, -1.22) * mm});
            skSolve(sketch);
        }
        {
            var Q0;
            Q0=qSketchRegion(id+"F10",true);
            extrude(context, id + "F11", {"entities" : qUnion([Q0]), "operationType" : NewBodyOperationType.ADD, "depth" : 9 * mm, "offsetDistance" : 25 * mm});
        }
        {
            var Q0;
            Q0=qCreatedBy(id+"F7.planeOp",FACE);
            var sketch = newSketch(context, id + "F12", { "sketchPlane" : qUnion([Q0])});
            skArc(sketch, "E22", {"start": v(9.85, -49.02) * mm, "mid": v(49.63, -6.1) * mm, "end": v(21.41, 45.18) * mm});
            skCircle(sketch, "E23", {"center": v(20.8, 0) * mm, "radius": 6.2 * mm});
            skCircle(sketch, "E24", {"center": v(0, 0) * mm, "radius": 11.3 * mm});
            skLineSegment(sketch, "E25", {"start": v(-22.92, 0) * mm, "end": v(21.41, 45.18) * mm});
            skLineSegment(sketch, "E26", {"start": v(-22.92, 0) * mm, "end": v(9.85, -49.02) * mm});
            skSolve(sketch);
        }
        {
            var Q0;
            Q0=qSketchRegion(id+"F12",true);
            extrude(context, id + "F13", {"entities" : qUnion([Q0]), "depth" : 1.5 * mm, "offsetDistance" : 25 * mm});
        }
        {
            var Q0;
            Q0=makeQuery(id+"F13.opExtrude","CAP_FACE",FACE,{"disambiguationData":[OSD([sQuery(id+"F12.wireOp",EDGE,"E22"),sQuery(id+"F12.wireOp",EDGE,"E23"),sQuery(id+"F12.wireOp",EDGE,"E24")])],"isStart":true});
            chamfer(context, id + "F14", {"entities" : qUnion([Q0]), "width" : .4 * mm, "tangentPropagation" : true});
        }
        {
            var Q0;
            Q0=makeQuery(id+"F13.opExtrude","CAP_FACE",FACE,{"disambiguationData":[OSD([sQuery(id+"F12.wireOp",EDGE,"E22"),sQuery(id+"F12.wireOp",EDGE,"E23"),sQuery(id+"F12.wireOp",EDGE,"E24")])],"isStart":false});
            var sketch = newSketch(context, id + "F15", { "sketchPlane" : qUnion([Q0])});
            skCircle(sketch, "E27", {"center": v(0, 0) * mm, "radius": 11.2 * mm});
            skCircle(sketch, "E28", {"center": v(0, 0) * mm, "radius": 13 * mm});
            skCircle(sketch, "E29", {"center": v(20.8, 0) * mm, "radius": 6.3 * mm});
            skCircle(sketch, "E30", {"center": v(20.8, 0) * mm, "radius": 8 * mm});
            skSolve(sketch);
        }
        {
            var Q0;
            Q0=qSketchRegion(id+"F15",true);
            extrude(context, id + "F16", {"entities" : qUnion([Q0]), "operationType" : NewBodyOperationType.ADD, "depth" : 7 * mm, "offsetDistance" : 25 * mm});
        }
        {
            var Q0;
            Q0=makeQuery(id+"F16.opExtrude","CAP_FACE",FACE,{"disambiguationData":[OSD([sQuery(id+"F15.wireOp",EDGE,"E27"),sQuery(id+"F15.wireOp",EDGE,"E28"),sQuery(id+"F15.wireOp",EDGE,"E29"),sQuery(id+"F15.wireOp",EDGE,"E30")])],"isStart":false});
            var sketch = newSketch(context, id + "F17", { "sketchPlane" : qUnion([Q0])});
            skCircle(sketch, "E31", {"center": v(0, 0) * mm, "radius": 11.2 * mm});
            skCircle(sketch, "E32", {"center": v(0, 0) * mm, "radius": 10.8 * mm});
            skSolve(sketch);
        }
        {
            var Q0;
            Q0 = qSketchRegion(id + "F17", true);
            extrude(context, id + "F18", {"entities" : qUnion([Q0]), "operationType" : NewBodyOperationType.ADD, "oppositeDirection" : true, "depth" : 1 * mm, "offsetDistance" : 25 * mm});
        }
        {
            var Q0;
            Q0=makeQuery(id+"F11.opExtrude","CAP_FACE",FACE,{"disambiguationData":[OSD([sQuery(id+"F10.wireOp",EDGE,"2d333abf-ac48-45f7-9fb1-957c00dd3a71"),sQuery(id+"F10.wireOp",EDGE,"c64c2ddc-d30f-4505-a8a8-bf3b5c701e5a.MirrorCS"),sQuery(id+"F10.wireOp",EDGE,"31d0e052-f0ee-4bec-8aed-0fbc6bf63170.1.0"),sQuery(id+"F10.wireOp",EDGE,"31d0e052-f0ee-4bec-8aed-0fbc6bf63170.1.1"),sQuery(id+"F10.wireOp",EDGE,"31d0e052-f0ee-4bec-8aed-0fbc6bf63170.2.0"),sQuery(id+"F10.wireOp",EDGE,"31d0e052-f0ee-4bec-8aed-0fbc6bf63170.2.1"),sQuery(id+"F10.wireOp",EDGE,"31d0e052-f0ee-4bec-8aed-0fbc6bf63170.3.0"),sQuery(id+"F10.wireOp",EDGE,"31d0e052-f0ee-4bec-8aed-0fbc6bf63170.3.1"),sQuery(id+"F10.wireOp",EDGE,"31d0e052-f0ee-4bec-8aed-0fbc6bf63170.4.0"),sQuery(id+"F10.wireOp",EDGE,"31d0e052-f0ee-4bec-8aed-0fbc6bf63170.4.1"),sQuery(id+"F10.wireOp",EDGE,"31d0e052-f0ee-4bec-8aed-0fbc6bf63170.5.0"),sQuery(id+"F10.wireOp",EDGE,"31d0e052-f0ee-4bec-8aed-0fbc6bf63170.5.1"),sQuery(id+"F10.wireOp",EDGE,"31d0e052-f0ee-4bec-8aed-0fbc6bf63170.6.0"),sQuery(id+"F10.wireOp",EDGE,"31d0e052-f0ee-4bec-8aed-0fbc6bf63170.6.1"),sQuery(id+"F10.wireOp",EDGE,"31d0e052-f0ee-4bec-8aed-0fbc6bf63170.7.0"),sQuery(id+"F10.wireOp",EDGE,"31d0e052-f0ee-4bec-8aed-0fbc6bf63170.7.1"),sQuery(id+"F10.wireOp",EDGE,"31d0e052-f0ee-4bec-8aed-0fbc6bf63170.8.0"),sQuery(id+"F10.wireOp",EDGE,"31d0e052-f0ee-4bec-8aed-0fbc6bf63170.8.1"),sQuery(id+"F10.wireOp",EDGE,"31d0e052-f0ee-4bec-8aed-0fbc6bf63170.9.0"),sQuery(id+"F10.wireOp",EDGE,"31d0e052-f0ee-4bec-8aed-0fbc6bf63170.9.1"),sQuery(id+"F10.wireOp",EDGE,"31d0e052-f0ee-4bec-8aed-0fbc6bf63170.10.0"),sQuery(id+"F10.wireOp",EDGE,"31d0e052-f0ee-4bec-8aed-0fbc6bf63170.10.1"),sQuery(id+"F10.wireOp",EDGE,"31d0e052-f0ee-4bec-8aed-0fbc6bf63170.11.0"),sQuery(id+"F10.wireOp",EDGE,"31d0e052-f0ee-4bec-8aed-0fbc6bf63170.11.1"),sQuery(id+"F10.wireOp",EDGE,"31d0e052-f0ee-4bec-8aed-0fbc6bf63170.12.0"),sQuery(id+"F10.wireOp",EDGE,"31d0e052-f0ee-4bec-8aed-0fbc6bf63170.12.1"),sQuery(id+"F10.wireOp",EDGE,"31d0e052-f0ee-4bec-8aed-0fbc6bf63170.13.0"),sQuery(id+"F10.wireOp",EDGE,"31d0e052-f0ee-4bec-8aed-0fbc6bf63170.13.1"),sQuery(id+"F10.wireOp",EDGE,"31d0e052-f0ee-4bec-8aed-0fbc6bf63170.14.0"),sQuery(id+"F10.wireOp",EDGE,"31d0e052-f0ee-4bec-8aed-0fbc6bf63170.14.1"),sQuery(id+"F10.wireOp",EDGE,"65c9d81a-f96d-433a-8740-731c835ab0f8.1.15.0"),sQuery(id+"F10.wireOp",EDGE,"65c9d81a-f96d-433a-8740-731c835ab0f8.3.15.0"),sQuery(id+"F10.wireOp",EDGE,"65c9d81a-f96d-433a-8740-731c835ab0f8.1.16.0"),sQuery(id+"F10.wireOp",EDGE,"65c9d81a-f96d-433a-8740-731c835ab0f8.3.16.0"),sQuery(id+"F10.wireOp",EDGE,"65c9d81a-f96d-433a-8740-731c835ab0f8.1.17.0"),sQuery(id+"F10.wireOp",EDGE,"65c9d81a-f96d-433a-8740-731c835ab0f8.3.17.0"),sQuery(id+"F10.wireOp",EDGE,"65c9d81a-f96d-433a-8740-731c835ab0f8.1.18.0"),sQuery(id+"F10.wireOp",EDGE,"65c9d81a-f96d-433a-8740-731c835ab0f8.3.18.0"),sQuery(id+"F10.wireOp",EDGE,"65c9d81a-f96d-433a-8740-731c835ab0f8.1.19.0"),sQuery(id+"F10.wireOp",EDGE,"65c9d81a-f96d-433a-8740-731c835ab0f8.3.19.0"),sQuery(id+"F10.wireOp",EDGE,"65c9d81a-f96d-433a-8740-731c835ab0f8.1.20.0"),sQuery(id+"F10.wireOp",EDGE,"65c9d81a-f96d-433a-8740-731c835ab0f8.3.20.0"),sQuery(id+"F10.wireOp",EDGE,"65c9d81a-f96d-433a-8740-731c835ab0f8.1.21.0"),sQuery(id+"F10.wireOp",EDGE,"65c9d81a-f96d-433a-8740-731c835ab0f8.3.21.0"),sQuery(id+"F10.wireOp",EDGE,"65c9d81a-f96d-433a-8740-731c835ab0f8.1.22.0"),sQuery(id+"F10.wireOp",EDGE,"65c9d81a-f96d-433a-8740-731c835ab0f8.3.22.0"),sQuery(id+"F10.wireOp",EDGE,"65c9d81a-f96d-433a-8740-731c835ab0f8.1.23.0"),sQuery(id+"F10.wireOp",EDGE,"65c9d81a-f96d-433a-8740-731c835ab0f8.3.23.0"),sQuery(id+"F10.wireOp",EDGE,"E17")])],"isStart":false});
            var Q1;
            Q1=makeQuery(id+"F16.opExtrude","CAP_EDGE",EDGE,{"disambiguationData":[OSD([sQuery(id+"F15.wireOp",EDGE,"E27")])],"isStart":true});
            chamfer(context, id + "F19", {"entities" : qUnion([Q0, Q1]), "width" : .4 * mm, "tangentPropagation" : true});
        }
        {
            var Q0;
            Q0=qCreatedBy(makeId("Front.planeOp"),FACE);
            var sketch = newSketch(context, id + "F20", { "sketchPlane" : qUnion([Q0])});
            skLineSegment(sketch, "E33", {"start": v(20.8, 0) * mm, "end": v(20.8, 30.23) * mm});
            skSolve(sketch);
        }
        {
            var Q0;
            {var subQ0=sQuery(id+"F12.wireOp",EDGE,"E22");Q0=makeQuery(id+"F16.boolean.opBoolean","SPLIT",FACE,{"disambiguationData":[TD([makeQuery(id+"F13.opExtrude","SWEPT_FACE",FACE,{"disambiguationData":[OSD([subQ0])]})])],"derivedFrom":makeQuery(id+"F13.opExtrude","CAP_FACE",FACE,{"disambiguationData":[OSD([subQ0,sQuery(id+"F12.wireOp",EDGE,"E23"),sQuery(id+"F12.wireOp",EDGE,"E24")])],"isStart":false})});}
            var sketch = newSketch(context, id + "F21", { "sketchPlane" : qUnion([Q0])});
            skLineSegment(sketch, "E34", {"start": v(20.8, 0) * mm, "end": v(20.8, 4.6) * mm});
            skCircle(sketch, "E35", {"center": v(16.3, 14.75) * mm, "radius": 1.47 * mm});
            skLineSegment(sketch, "E36.bottom", {"start": v(31.8, 10.75) * mm, "end": v(9.8, 10.75) * mm});
            skLineSegment(sketch, "E36.top", {"start": v(31.8, 18.75) * mm, "end": v(9.8, 18.75) * mm});
            skLineSegment(sketch, "E36.left", {"start": v(31.8, 10.75) * mm, "end": v(31.8, 18.75) * mm});
            skLineSegment(sketch, "E36.right", {"start": v(9.8, 10.75) * mm, "end": v(9.8, 18.75) * mm});
            skPoint(sketch, "E36.middle", {"position": v(20.8, 14.75) * mm});
            skCircle(sketch, "E37.MirrorC", {"center": v(25.3, 14.75) * mm, "radius": 1.47 * mm});
            skPoint(sketch, "E38", {"position": v(20.8, -9.75) * mm});
            skLineSegment(sketch, "E39", {"start": v(20.8, -9.75) * mm, "end": v(16.6, -9.75) * mm});
            skPoint(sketch, "E40.MirrorP", {"position": v(20.8, -34.25) * mm});
            skLineSegment(sketch, "E41.MirrorCS", {"start": v(9.8, -30.25) * mm, "end": v(9.8, -38.25) * mm});
            skLineSegment(sketch, "E42.MirrorCS", {"start": v(31.8, -38.25) * mm, "end": v(9.8, -38.25) * mm});
            skLineSegment(sketch, "E43.MirrorCS", {"start": v(31.8, -30.25) * mm, "end": v(9.8, -30.25) * mm});
            skCircle(sketch, "E44.MirrorC", {"center": v(25.3, -34.25) * mm, "radius": 1.47 * mm});
            skLineSegment(sketch, "E45.MirrorCS", {"start": v(31.8, -30.25) * mm, "end": v(31.8, -38.25) * mm});
            skCircle(sketch, "E46.MirrorC", {"center": v(16.3, -34.25) * mm, "radius": 1.47 * mm});
            skSolve(sketch);
        }
        {
            var Q0;
            Q0 = qSketchRegion(id + "F21", true);
            extrude(context, id + "F22", {"entities" : qUnion([Q0]), "operationType" : NewBodyOperationType.ADD, "depth" : 18 * mm, "offsetDistance" : 25 * mm});
        }
    });
